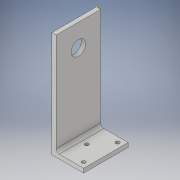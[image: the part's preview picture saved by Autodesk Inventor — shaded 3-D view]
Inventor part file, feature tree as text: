
AUTODESK INVENTOR PART (.ipt)
format: ipt  version: 2017 (Build 210142000, 142)  size: 129,536 bytes
history: native  units: in
note: dims shown in document units (in); Inventor stores cm internally (conversion verified against a paired STEP export)
features: sketch x4, extrude x3, fillet x1
ambient origin geometry x8: Origin, YZ Plane, XZ Plane, XY Plane, X Axis, Y Axis, Z Axis, Center Point
bodies: Solid1 (feature_tree)
feature tree (8):
  sketch  "Sketch1"  dims[d0=3.937in d1=1.1811in]
  extrude  "Extrusion1"  Depth=1.1811in
  extrude  "Extrusion3"  Depth=1.0236in
  fillet  "Fillet1"  Radius=1.6535in
  extrude  "Extrusion4"  Depth=0.1378in
  sketch  "Sketch2"  dims[d2=0.1575in d3=1.0236in d4=1.6535in d5=0.0in]
  sketch  "Sketch4"  dims[d11=0.1378in d12=0.1378in]
  sketch  "Sketch5"  dims[d13=0.1378in d14=0.1969in d15=0.1969in d16=0.1969in d17=0.1969in d18=0.4724in d19=0.8268in d20=0.1575in d21=0.0in d22=0.1181in d23=0.5354in d24=0.8268in d25=0.8268in d26=0.1575in d27=0.0in]
